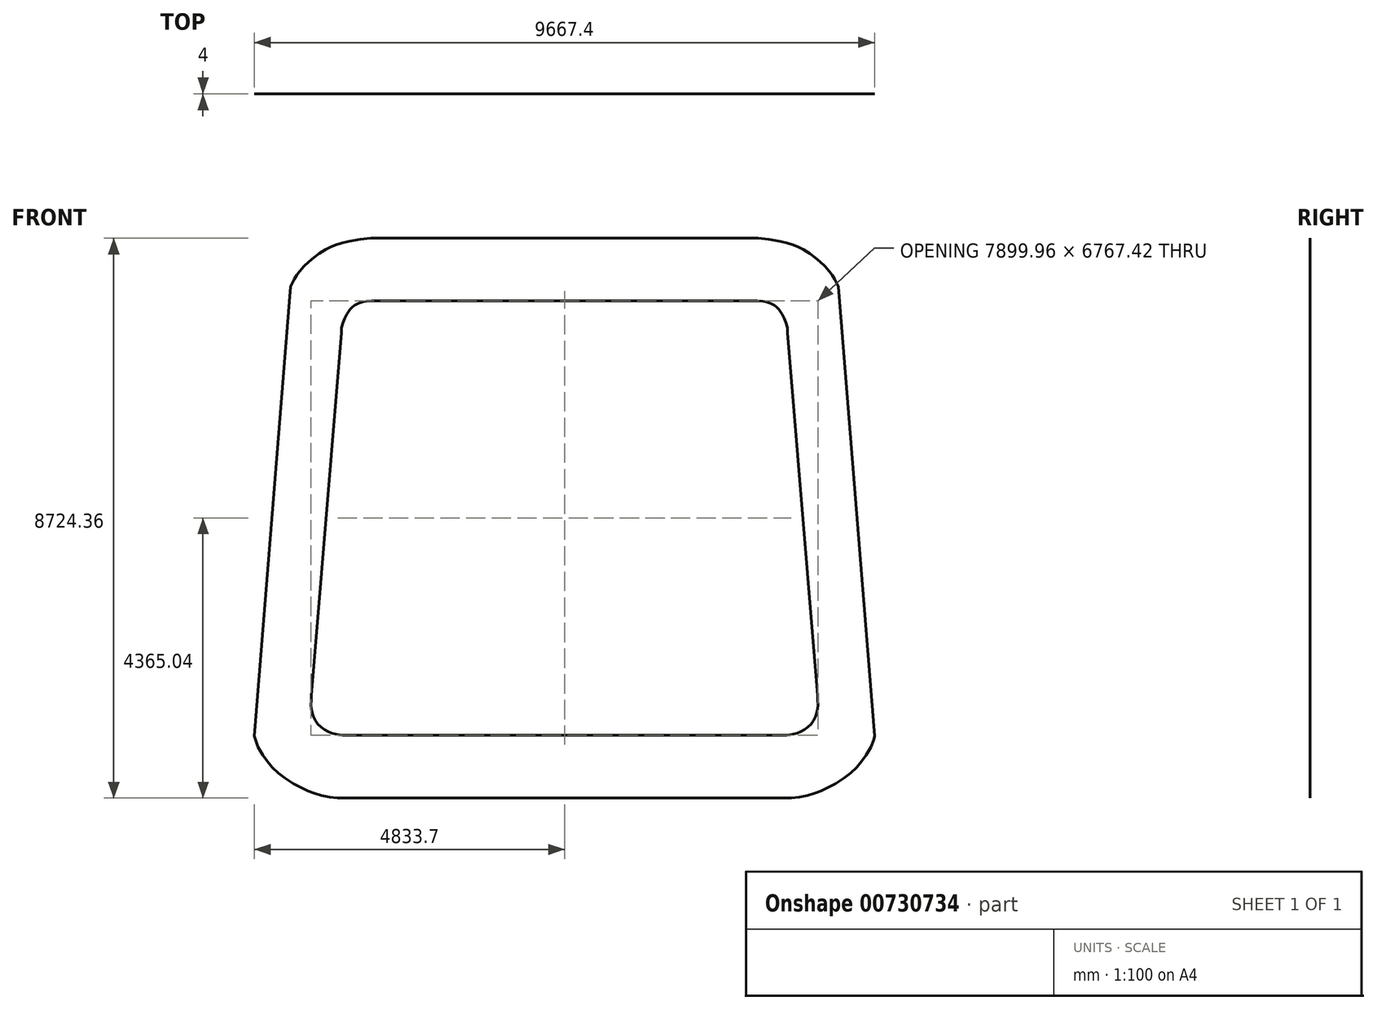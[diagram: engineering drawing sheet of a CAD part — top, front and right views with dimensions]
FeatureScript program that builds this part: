
annotation { "Feature Type Name" : "Feature", "Feature Type Description" : "" }
export const myFeature = defineFeature(function(context is Context, id is Id, definition is map)
    precondition{}
    {
        {
            var Q0;
            Q0=qCreatedBy(makeId("Front.planeOp"),FACE);
            var sketch = newSketch(context, id + "F0", { "sketchPlane" : qUnion([Q0])});
            skLineSegment(sketch, "E0", {"start": v(0, 3384.82) * mm, "end": v(0, 3257.82) * mm});
            skLineSegment(sketch, "E1", {"start": v(0, 3257.82) * mm, "end": v(0, 3384.82) * mm});
            skLineSegment(sketch, "E2", {"start": v(0, 3384.82) * mm, "end": v(1097.08, 3384.82) * mm});
            skLineSegment(sketch, "E3", {"start": v(1097.08, 3384.82) * mm, "end": v(2926.54, 3384.82) * mm});
            skLineSegment(sketch, "E4", {"start": v(2926.54, 3384.82) * mm, "end": v(2926.54, 3257.82) * mm});
            skLineSegment(sketch, "E5", {"start": v(2926.54, 3257.82) * mm, "end": v(2926.54, 3384.82) * mm});
            skLineSegment(sketch, "E6", {"start": v(2926.54, 3384.82) * mm, "end": v(3003.47, 3386.57) * mm});
            skLineSegment(sketch, "E7", {"start": v(3003.47, 3386.57) * mm, "end": v(3087.27, 3381.54) * mm});
            skLineSegment(sketch, "E8", {"start": v(3087.27, 3381.54) * mm, "end": v(3136.27, 3373.95) * mm});
            skLineSegment(sketch, "E9", {"start": v(3136.27, 3373.95) * mm, "end": v(3212.1, 3352.1) * mm});
            skLineSegment(sketch, "E10", {"start": v(3212.1, 3352.1) * mm, "end": v(3270.96, 3319.61) * mm});
            skLineSegment(sketch, "E11", {"start": v(3270.96, 3319.61) * mm, "end": v(3307.46, 3290.35) * mm});
            skLineSegment(sketch, "E12", {"start": v(3307.46, 3290.35) * mm, "end": v(3340.25, 3256.95) * mm});
            skLineSegment(sketch, "E13", {"start": v(3340.25, 3256.95) * mm, "end": v(3397.25, 3177.37) * mm});
            skLineSegment(sketch, "E14", {"start": v(3397.25, 3177.37) * mm, "end": v(3428.29, 3116.11) * mm});
            skLineSegment(sketch, "E15", {"start": v(3428.29, 3116.11) * mm, "end": v(3452.77, 3051.82) * mm});
            skLineSegment(sketch, "E16", {"start": v(3452.77, 3051.82) * mm, "end": v(3473.68, 2969.12) * mm});
            skLineSegment(sketch, "E17", {"start": v(3473.68, 2969.12) * mm, "end": v(3479.27, 2893.07) * mm});
            skLineSegment(sketch, "E18", {"start": v(3479.27, 2893.07) * mm, "end": v(3352.6, 2883.8) * mm});
            skLineSegment(sketch, "E19", {"start": v(3352.6, 2883.8) * mm, "end": v(3479.27, 2893.07) * mm});
            skLineSegment(sketch, "E20", {"start": v(3479.27, 2893.07) * mm, "end": v(3946.7, -2766.33) * mm});
            skLineSegment(sketch, "E21", {"start": v(3946.7, -2766.33) * mm, "end": v(3820.13, -2776.8) * mm});
            skLineSegment(sketch, "E22", {"start": v(3820.13, -2776.8) * mm, "end": v(3946.7, -2766.33) * mm});
            skLineSegment(sketch, "E23", {"start": v(3946.7, -2766.33) * mm, "end": v(3949.2, -2835.39) * mm});
            skLineSegment(sketch, "E24", {"start": v(3949.2, -2835.39) * mm, "end": v(3949.98, -2911.72) * mm});
            skLineSegment(sketch, "E25", {"start": v(3949.98, -2911.72) * mm, "end": v(3944.92, -2970.67) * mm});
            skLineSegment(sketch, "E26", {"start": v(3944.92, -2970.67) * mm, "end": v(3933.8, -3028.94) * mm});
            skLineSegment(sketch, "E27", {"start": v(3933.8, -3028.94) * mm, "end": v(3914.14, -3091.93) * mm});
            skLineSegment(sketch, "E28", {"start": v(3914.14, -3091.93) * mm, "end": v(3885.64, -3151.26) * mm});
            skLineSegment(sketch, "E29", {"start": v(3885.64, -3151.26) * mm, "end": v(3844.67, -3208.36) * mm});
            skLineSegment(sketch, "E30", {"start": v(3844.67, -3208.36) * mm, "end": v(3794.43, -3257.72) * mm});
            skLineSegment(sketch, "E31", {"start": v(3794.43, -3257.72) * mm, "end": v(3743.25, -3294.67) * mm});
            skLineSegment(sketch, "E32", {"start": v(3743.25, -3294.67) * mm, "end": v(3687.8, -3324.85) * mm});
            skLineSegment(sketch, "E33", {"start": v(3687.8, -3324.85) * mm, "end": v(3631.13, -3348.09) * mm});
            skLineSegment(sketch, "E34", {"start": v(3631.13, -3348.09) * mm, "end": v(3572.36, -3365.28) * mm});
            skLineSegment(sketch, "E35", {"start": v(3572.36, -3365.28) * mm, "end": v(3517.09, -3375.67) * mm});
            skLineSegment(sketch, "E36", {"start": v(3517.09, -3375.67) * mm, "end": v(3461.16, -3380.85) * mm});
            skLineSegment(sketch, "E37", {"start": v(3461.16, -3380.85) * mm, "end": v(3449.42, -3254.39) * mm});
            skLineSegment(sketch, "E38", {"start": v(3449.42, -3254.39) * mm, "end": v(3461.16, -3380.85) * mm});
            skLineSegment(sketch, "E39", {"start": v(3461.16, -3380.85) * mm, "end": v(0, -3380.85) * mm});
            skLineSegment(sketch, "E40", {"start": v(0, -3380.85) * mm, "end": v(0, -3253.85) * mm});
            skLineSegment(sketch, "E41", {"start": v(0, -3253.85) * mm, "end": v(0, -3380.85) * mm});
            skLineSegment(sketch, "E42", {"start": v(0, -3380.85) * mm, "end": v(-3461.16, -3380.85) * mm});
            skLineSegment(sketch, "E43", {"start": v(-3461.16, -3380.85) * mm, "end": v(-3461.16, -3253.85) * mm});
            skLineSegment(sketch, "E44", {"start": v(-3461.16, -3253.85) * mm, "end": v(-3461.16, -3380.85) * mm});
            skLineSegment(sketch, "E45", {"start": v(-3461.16, -3380.85) * mm, "end": v(-3517.09, -3375.67) * mm});
            skLineSegment(sketch, "E46", {"start": v(-3517.09, -3375.67) * mm, "end": v(-3572.36, -3365.28) * mm});
            skLineSegment(sketch, "E47", {"start": v(-3572.36, -3365.28) * mm, "end": v(-3631.13, -3348.09) * mm});
            skLineSegment(sketch, "E48", {"start": v(-3631.13, -3348.09) * mm, "end": v(-3687.8, -3324.85) * mm});
            skLineSegment(sketch, "E49", {"start": v(-3687.8, -3324.85) * mm, "end": v(-3743.25, -3294.67) * mm});
            skLineSegment(sketch, "E50", {"start": v(-3743.25, -3294.67) * mm, "end": v(-3794.43, -3257.72) * mm});
            skLineSegment(sketch, "E51", {"start": v(-3794.43, -3257.72) * mm, "end": v(-3844.67, -3208.36) * mm});
            skLineSegment(sketch, "E52", {"start": v(-3844.67, -3208.36) * mm, "end": v(-3885.64, -3151.26) * mm});
            skLineSegment(sketch, "E53", {"start": v(-3885.64, -3151.26) * mm, "end": v(-3914.14, -3091.93) * mm});
            skLineSegment(sketch, "E54", {"start": v(-3914.14, -3091.93) * mm, "end": v(-3933.8, -3028.94) * mm});
            skLineSegment(sketch, "E55", {"start": v(-3933.8, -3028.94) * mm, "end": v(-3944.92, -2970.67) * mm});
            skLineSegment(sketch, "E56", {"start": v(-3944.92, -2970.67) * mm, "end": v(-3949.98, -2911.72) * mm});
            skLineSegment(sketch, "E57", {"start": v(-3949.98, -2911.72) * mm, "end": v(-3949.2, -2835.39) * mm});
            skLineSegment(sketch, "E58", {"start": v(-3949.2, -2835.39) * mm, "end": v(-3946.7, -2766.33) * mm});
            skLineSegment(sketch, "E59", {"start": v(-3946.7, -2766.33) * mm, "end": v(-3819.78, -2770.92) * mm});
            skLineSegment(sketch, "E60", {"start": v(-3819.78, -2770.92) * mm, "end": v(-3946.7, -2766.33) * mm});
            skLineSegment(sketch, "E61", {"start": v(-3946.7, -2766.33) * mm, "end": v(-3479.27, 2893.07) * mm});
            skLineSegment(sketch, "E62", {"start": v(-3479.27, 2893.07) * mm, "end": v(-3352.7, 2882.63) * mm});
            skLineSegment(sketch, "E63", {"start": v(-3352.7, 2882.63) * mm, "end": v(-3479.27, 2893.07) * mm});
            skLineSegment(sketch, "E64", {"start": v(-3479.27, 2893.07) * mm, "end": v(-3473.68, 2969.12) * mm});
            skLineSegment(sketch, "E65", {"start": v(-3473.68, 2969.12) * mm, "end": v(-3452.77, 3051.82) * mm});
            skLineSegment(sketch, "E66", {"start": v(-3452.77, 3051.82) * mm, "end": v(-3428.29, 3116.11) * mm});
            skLineSegment(sketch, "E67", {"start": v(-3428.29, 3116.11) * mm, "end": v(-3397.25, 3177.37) * mm});
            skLineSegment(sketch, "E68", {"start": v(-3397.25, 3177.37) * mm, "end": v(-3340.25, 3256.95) * mm});
            skLineSegment(sketch, "E69", {"start": v(-3340.25, 3256.95) * mm, "end": v(-3307.46, 3290.35) * mm});
            skLineSegment(sketch, "E70", {"start": v(-3307.46, 3290.35) * mm, "end": v(-3270.96, 3319.61) * mm});
            skLineSegment(sketch, "E71", {"start": v(-3270.96, 3319.61) * mm, "end": v(-3212.1, 3352.1) * mm});
            skLineSegment(sketch, "E72", {"start": v(-3212.1, 3352.1) * mm, "end": v(-3136.27, 3373.95) * mm});
            skLineSegment(sketch, "E73", {"start": v(-3136.27, 3373.95) * mm, "end": v(-3087.27, 3381.54) * mm});
            skLineSegment(sketch, "E74", {"start": v(-3087.27, 3381.54) * mm, "end": v(-3003.47, 3386.57) * mm});
            skLineSegment(sketch, "E75", {"start": v(-3003.47, 3386.57) * mm, "end": v(-2926.54, 3384.82) * mm});
            skLineSegment(sketch, "E76", {"start": v(-2926.54, 3384.82) * mm, "end": v(-2929.43, 3257.84) * mm});
            skLineSegment(sketch, "E77", {"start": v(-2929.43, 3257.84) * mm, "end": v(-2926.54, 3384.82) * mm});
            skLineSegment(sketch, "E78", {"start": v(-2926.54, 3384.82) * mm, "end": v(-1097.08, 3384.82) * mm});
            skLineSegment(sketch, "E79", {"start": v(-1097.08, 3384.82) * mm, "end": v(0, 3384.82) * mm});
            skLineSegment(sketch, "E80", {"start": v(0, 4362.18) * mm, "end": v(0, 4235.18) * mm});
            skLineSegment(sketch, "E81", {"start": v(0, 4235.18) * mm, "end": v(0, 4362.18) * mm});
            skLineSegment(sketch, "E82", {"start": v(0, 4362.18) * mm, "end": v(1600.56, 4362.18) * mm});
            skLineSegment(sketch, "E83", {"start": v(1600.56, 4362.18) * mm, "end": v(3020.97, 4362.18) * mm});
            skLineSegment(sketch, "E84", {"start": v(3020.97, 4362.18) * mm, "end": v(3020.97, 4235.18) * mm});
            skLineSegment(sketch, "E85", {"start": v(3020.97, 4235.18) * mm, "end": v(3020.97, 4362.18) * mm});
            skLineSegment(sketch, "E86", {"start": v(3020.97, 4362.18) * mm, "end": v(3187.57, 4344.43) * mm});
            skLineSegment(sketch, "E87", {"start": v(3187.57, 4344.43) * mm, "end": v(3362.2, 4315.02) * mm});
            skLineSegment(sketch, "E88", {"start": v(3362.2, 4315.02) * mm, "end": v(3467.28, 4288.93) * mm});
            skLineSegment(sketch, "E89", {"start": v(3467.28, 4288.93) * mm, "end": v(3570.45, 4255.78) * mm});
            skLineSegment(sketch, "E90", {"start": v(3570.45, 4255.78) * mm, "end": v(3649.42, 4224.57) * mm});
            skLineSegment(sketch, "E91", {"start": v(3649.42, 4224.57) * mm, "end": v(3725.55, 4187.25) * mm});
            skLineSegment(sketch, "E92", {"start": v(3725.55, 4187.25) * mm, "end": v(3828.9, 4121.62) * mm});
            skLineSegment(sketch, "E93", {"start": v(3828.9, 4121.62) * mm, "end": v(3909.92, 4060.84) * mm});
            skLineSegment(sketch, "E94", {"start": v(3909.92, 4060.84) * mm, "end": v(3987.16, 3995.3) * mm});
            skLineSegment(sketch, "E95", {"start": v(3987.16, 3995.3) * mm, "end": v(4061.03, 3923.88) * mm});
            skLineSegment(sketch, "E96", {"start": v(4061.03, 3923.88) * mm, "end": v(4128.62, 3846.64) * mm});
            skLineSegment(sketch, "E97", {"start": v(4128.62, 3846.64) * mm, "end": v(4172.48, 3786.7) * mm});
            skLineSegment(sketch, "E98", {"start": v(4172.48, 3786.7) * mm, "end": v(4211.73, 3723.58) * mm});
            skLineSegment(sketch, "E99", {"start": v(4211.73, 3723.58) * mm, "end": v(4268.27, 3607.7) * mm});
            skLineSegment(sketch, "E100", {"start": v(4268.27, 3607.7) * mm, "end": v(4154.12, 3552.02) * mm});
            skLineSegment(sketch, "E101", {"start": v(4154.12, 3552.02) * mm, "end": v(4268.27, 3607.7) * mm});
            skLineSegment(sketch, "E102", {"start": v(4268.27, 3607.7) * mm, "end": v(4833.7, -3395.71) * mm});
            skLineSegment(sketch, "E103", {"start": v(4833.7, -3395.71) * mm, "end": v(4707.1, -3405.92) * mm});
            skLineSegment(sketch, "E104", {"start": v(4707.1, -3405.92) * mm, "end": v(4833.7, -3395.71) * mm});
            skLineSegment(sketch, "E105", {"start": v(4833.7, -3395.71) * mm, "end": v(4819.68, -3452.79) * mm});
            skLineSegment(sketch, "E106", {"start": v(4819.68, -3452.79) * mm, "end": v(4775.68, -3564.8) * mm});
            skLineSegment(sketch, "E107", {"start": v(4775.68, -3564.8) * mm, "end": v(4702.43, -3694.85) * mm});
            skLineSegment(sketch, "E108", {"start": v(4702.43, -3694.85) * mm, "end": v(4633.11, -3791.12) * mm});
            skLineSegment(sketch, "E109", {"start": v(4633.11, -3791.12) * mm, "end": v(4555.13, -3880.62) * mm});
            skLineSegment(sketch, "E110", {"start": v(4555.13, -3880.62) * mm, "end": v(4462.02, -3969.32) * mm});
            skLineSegment(sketch, "E111", {"start": v(4462.02, -3969.32) * mm, "end": v(4361.2, -4049.15) * mm});
            skLineSegment(sketch, "E112", {"start": v(4361.2, -4049.15) * mm, "end": v(4228.16, -4135.62) * mm});
            skLineSegment(sketch, "E113", {"start": v(4228.16, -4135.62) * mm, "end": v(4087.93, -4210.14) * mm});
            skLineSegment(sketch, "E114", {"start": v(4087.93, -4210.14) * mm, "end": v(3998.11, -4250.86) * mm});
            skLineSegment(sketch, "E115", {"start": v(3998.11, -4250.86) * mm, "end": v(3906.09, -4286.06) * mm});
            skLineSegment(sketch, "E116", {"start": v(3906.09, -4286.06) * mm, "end": v(3786.28, -4320.9) * mm});
            skLineSegment(sketch, "E117", {"start": v(3786.28, -4320.9) * mm, "end": v(3663.75, -4344.7) * mm});
            skLineSegment(sketch, "E118", {"start": v(3663.75, -4344.7) * mm, "end": v(3537.79, -4357.76) * mm});
            skLineSegment(sketch, "E119", {"start": v(3537.79, -4357.76) * mm, "end": v(3524.73, -4231.42) * mm});
            skLineSegment(sketch, "E120", {"start": v(3524.73, -4231.42) * mm, "end": v(3537.79, -4357.76) * mm});
            skLineSegment(sketch, "E121", {"start": v(3537.79, -4357.76) * mm, "end": v(0, -4362.18) * mm});
            skLineSegment(sketch, "E122", {"start": v(0, -4362.18) * mm, "end": v(-0.15, -4235.18) * mm});
            skLineSegment(sketch, "E123", {"start": v(-0.15, -4235.18) * mm, "end": v(0, -4362.18) * mm});
            skLineSegment(sketch, "E124", {"start": v(0, -4362.18) * mm, "end": v(-3537.79, -4357.76) * mm});
            skLineSegment(sketch, "E125", {"start": v(-3537.79, -4357.76) * mm, "end": v(-3537.64, -4230.76) * mm});
            skLineSegment(sketch, "E126", {"start": v(-3537.64, -4230.76) * mm, "end": v(-3537.79, -4357.76) * mm});
            skLineSegment(sketch, "E127", {"start": v(-3537.79, -4357.76) * mm, "end": v(-3663.75, -4344.7) * mm});
            skLineSegment(sketch, "E128", {"start": v(-3663.75, -4344.7) * mm, "end": v(-3786.28, -4320.9) * mm});
            skLineSegment(sketch, "E129", {"start": v(-3786.28, -4320.9) * mm, "end": v(-3906.09, -4286.06) * mm});
            skLineSegment(sketch, "E130", {"start": v(-3906.09, -4286.06) * mm, "end": v(-3998.11, -4250.86) * mm});
            skLineSegment(sketch, "E131", {"start": v(-3998.11, -4250.86) * mm, "end": v(-4087.93, -4210.14) * mm});
            skLineSegment(sketch, "E132", {"start": v(-4087.93, -4210.14) * mm, "end": v(-4228.16, -4135.62) * mm});
            skLineSegment(sketch, "E133", {"start": v(-4228.16, -4135.62) * mm, "end": v(-4361.2, -4049.15) * mm});
            skLineSegment(sketch, "E134", {"start": v(-4361.2, -4049.15) * mm, "end": v(-4462.02, -3969.32) * mm});
            skLineSegment(sketch, "E135", {"start": v(-4462.02, -3969.32) * mm, "end": v(-4555.13, -3880.62) * mm});
            skLineSegment(sketch, "E136", {"start": v(-4555.13, -3880.62) * mm, "end": v(-4633.11, -3791.12) * mm});
            skLineSegment(sketch, "E137", {"start": v(-4633.11, -3791.12) * mm, "end": v(-4702.43, -3694.85) * mm});
            skLineSegment(sketch, "E138", {"start": v(-4702.43, -3694.85) * mm, "end": v(-4775.68, -3564.8) * mm});
            skLineSegment(sketch, "E139", {"start": v(-4775.68, -3564.8) * mm, "end": v(-4819.68, -3452.79) * mm});
            skLineSegment(sketch, "E140", {"start": v(-4819.68, -3452.79) * mm, "end": v(-4833.7, -3395.71) * mm});
            skLineSegment(sketch, "E141", {"start": v(-4833.7, -3395.71) * mm, "end": v(-4710.35, -3365.41) * mm});
            skLineSegment(sketch, "E142", {"start": v(-4710.35, -3365.41) * mm, "end": v(-4833.7, -3395.71) * mm});
            skLineSegment(sketch, "E143", {"start": v(-4833.7, -3395.71) * mm, "end": v(-4268.27, 3607.7) * mm});
            skLineSegment(sketch, "E144", {"start": v(-4268.27, 3607.7) * mm, "end": v(-4141.67, 3597.5) * mm});
            skLineSegment(sketch, "E145", {"start": v(-4141.67, 3597.5) * mm, "end": v(-4268.27, 3607.7) * mm});
            skLineSegment(sketch, "E146", {"start": v(-4268.27, 3607.7) * mm, "end": v(-4211.73, 3723.58) * mm});
            skLineSegment(sketch, "E147", {"start": v(-4211.73, 3723.58) * mm, "end": v(-4172.48, 3786.7) * mm});
            skLineSegment(sketch, "E148", {"start": v(-4172.48, 3786.7) * mm, "end": v(-4128.62, 3846.64) * mm});
            skLineSegment(sketch, "E149", {"start": v(-4128.62, 3846.64) * mm, "end": v(-4061.03, 3923.88) * mm});
            skLineSegment(sketch, "E150", {"start": v(-4061.03, 3923.88) * mm, "end": v(-3987.14, 3995.3) * mm});
            skLineSegment(sketch, "E151", {"start": v(-3987.14, 3995.3) * mm, "end": v(-3909.9, 4060.84) * mm});
            skLineSegment(sketch, "E152", {"start": v(-3909.9, 4060.84) * mm, "end": v(-3828.9, 4121.62) * mm});
            skLineSegment(sketch, "E153", {"start": v(-3828.9, 4121.62) * mm, "end": v(-3725.52, 4187.25) * mm});
            skLineSegment(sketch, "E154", {"start": v(-3725.52, 4187.25) * mm, "end": v(-3649.42, 4224.57) * mm});
            skLineSegment(sketch, "E155", {"start": v(-3649.42, 4224.57) * mm, "end": v(-3570.45, 4255.78) * mm});
            skLineSegment(sketch, "E156", {"start": v(-3570.45, 4255.78) * mm, "end": v(-3467.28, 4288.93) * mm});
            skLineSegment(sketch, "E157", {"start": v(-3467.28, 4288.93) * mm, "end": v(-3362.2, 4315.02) * mm});
            skLineSegment(sketch, "E158", {"start": v(-3362.2, 4315.02) * mm, "end": v(-3187.57, 4344.43) * mm});
            skLineSegment(sketch, "E159", {"start": v(-3187.57, 4344.43) * mm, "end": v(-3020.97, 4362.18) * mm});
            skLineSegment(sketch, "E160", {"start": v(-3020.97, 4362.18) * mm, "end": v(-3007.51, 4235.9) * mm});
            skLineSegment(sketch, "E161", {"start": v(-3007.51, 4235.9) * mm, "end": v(-3020.97, 4362.18) * mm});
            skLineSegment(sketch, "E162", {"start": v(-3020.97, 4362.18) * mm, "end": v(-1600.56, 4362.18) * mm});
            skLineSegment(sketch, "E163", {"start": v(-1600.56, 4362.18) * mm, "end": v(0, 4362.18) * mm});
            skSolve(sketch);
        }
        {
            var Q0;
            Q0 = qSketchRegion(id + "F0", true);
            extrude(context, id + "F1", {"entities" : qUnion([Q0]), "depth" : 4 * mm, "offsetDistance" : 25 * mm});
        }
    });
